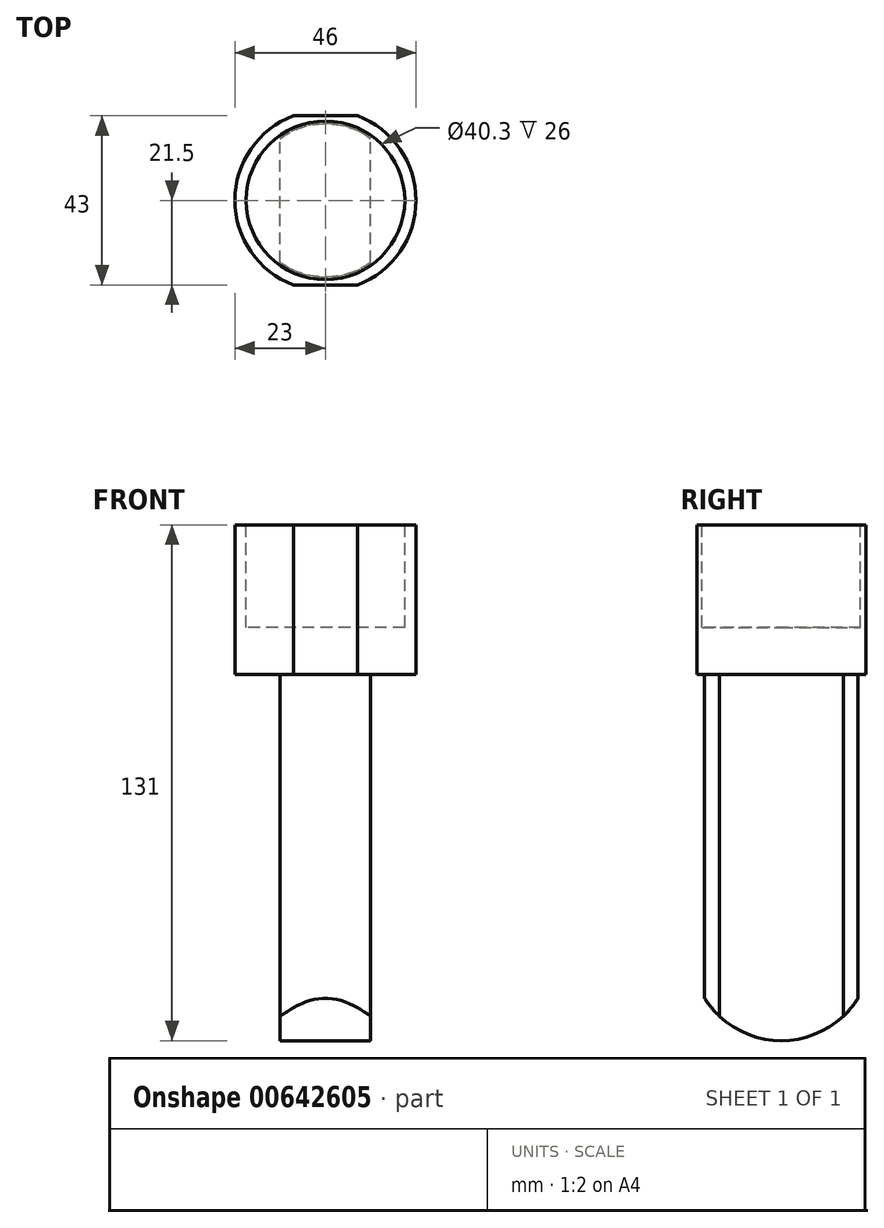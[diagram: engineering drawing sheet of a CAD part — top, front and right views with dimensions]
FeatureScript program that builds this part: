
annotation { "Feature Type Name" : "Feature", "Feature Type Description" : "" }
export const myFeature = defineFeature(function(context is Context, id is Id, definition is map)
    precondition{}
    {
        {
            var Q0;
            Q0=qCreatedBy(makeId("Top.planeOp"),FACE);
            var sketch = newSketch(context, id + "F0", { "sketchPlane" : qUnion([Q0])});
            skArc(sketch, "E0", {"start": v(-8.17, 21.5) * mm, "mid": v(-23, 0) * mm, "end": v(-8.17, -21.5) * mm});
            skLineSegment(sketch, "E1", {"start": v(-8.17, 21.5) * mm, "end": v(8.17, 21.5) * mm});
            skLineSegment(sketch, "E2.MirrorCS", {"start": v(-8.17, -21.5) * mm, "end": v(8.17, -21.5) * mm});
            skArc(sketch, "E3.trimOffspring", {"start": v(8.17, -21.5) * mm, "mid": v(23, 0) * mm, "end": v(8.17, 21.5) * mm});
            skSolve(sketch);
        }
        {
            var Q0;
            Q0 = qSketchRegion(id + "F0", true);
            extrude(context, id + "F1", {"entities" : qUnion([Q0]), "depth" : 38 * mm, "offsetDistance" : 25 * mm});
        }
        {
            var Q0;
            Q0=makeQuery(id+"F1.opExtrude","CAP_FACE",FACE,{"disambiguationData":[OSD([sQuery(id+"F0.wireOp",EDGE,"E0"),sQuery(id+"F0.wireOp",EDGE,"E1"),sQuery(id+"F0.wireOp",EDGE,"E2.MirrorCS"),sQuery(id+"F0.wireOp",EDGE,"E3.trimOffspring")])],"isStart":false});
            var sketch = newSketch(context, id + "F2", { "sketchPlane" : qUnion([Q0])});
            skCircle(sketch, "E4", {"center": v(0, 0) * mm, "radius": 20.15 * mm});
            skSolve(sketch);
        }
        {
            var Q0;
            Q0=makeQuery(id+"F2.imprint","IMPRINT",FACE,{"disambiguationData":[TD([[makeQuery(id+"F2.imprint","IMPRINT",EDGE,{"derivedFrom":sQuery(id+"F2.wireOp",EDGE,"E4")}),1.0]])]});
            extrude(context, id + "F3", {"entities" : qUnion([Q0]), "operationType" : NewBodyOperationType.REMOVE, "oppositeDirection" : true, "depth" : 26 * mm, "offsetDistance" : 25 * mm});
        }
        {
            var Q0;
            Q0=makeQuery(id+"F1.opExtrude","CAP_FACE",FACE,{"disambiguationData":[OSD([sQuery(id+"F0.wireOp",EDGE,"E0"),sQuery(id+"F0.wireOp",EDGE,"E1"),sQuery(id+"F0.wireOp",EDGE,"E2.MirrorCS"),sQuery(id+"F0.wireOp",EDGE,"E3.trimOffspring")])],"isStart":true});
            var sketch = newSketch(context, id + "F4", { "sketchPlane" : qUnion([Q0])});
            skArc(sketch, "E5", {"start": v(11.5, 15.75) * mm, "mid": v(0, 19.5) * mm, "end": v(-11.5, 15.75) * mm});
            skLineSegment(sketch, "E6", {"start": v(-11.5, 15.75) * mm, "end": v(-11.5, -15.75) * mm});
            skLineSegment(sketch, "E7.MirrorCS", {"start": v(11.5, 15.75) * mm, "end": v(11.5, -15.75) * mm});
            skArc(sketch, "E8.trimOffspring", {"start": v(-11.5, -15.75) * mm, "mid": v(0, -19.5) * mm, "end": v(11.5, -15.75) * mm});
            skSolve(sketch);
        }
        {
            var Q0;
            Q0=makeQuery(id+"F4.imprint","IMPRINT",FACE,{"disambiguationData":[TD([[makeQuery(id+"F4.imprint","IMPRINT",EDGE,{"derivedFrom":sQuery(id+"F4.wireOp",EDGE,"E5")}),1.0]])]});
            extrude(context, id + "F5", {"entities" : qUnion([Q0]), "operationType" : NewBodyOperationType.ADD, "depth" : 93 * mm, "offsetDistance" : 25 * mm});
        }
        {
            var Q0;
            Q0=makeQuery(id+"F5.opExtrude","SWEPT_FACE",FACE,{"disambiguationData":[OSD([sQuery(id+"F4.wireOp",EDGE,"E7.MirrorCS")])]});
            var sketch = newSketch(context, id + "F6", { "sketchPlane" : qUnion([Q0])});
            skArc(sketch, "E9", {"start": v(-22.95, -68.43) * mm, "mid": v(-5.38, -92.36) * mm, "end": v(21.15, -79.04) * mm});
            skLineSegment(sketch, "E10", {"start": v(-22.95, -68.43) * mm, "end": v(-27.64, -129.07) * mm});
            skLineSegment(sketch, "E11", {"start": v(-27.64, -129.07) * mm, "end": v(47.57, -125.6) * mm});
            skLineSegment(sketch, "E12", {"start": v(47.57, -125.6) * mm, "end": v(21.15, -79.04) * mm});
            skSolve(sketch);
        }
        {
            var Q0;
            {var subQ0=sQuery(id+"F6.wireOp",EDGE,"E9");var subQ1=sQuery(id+"F4.wireOp",EDGE,"E7.MirrorCS");var subQ4=makeQuery(id+"F5.opExtrude","CAP_EDGE",EDGE,{"disambiguationData":[OSD([subQ1])],"isStart":false});var subQ5=makeQuery(id+"F6.imprint","INTERSECT",VERTEX,{"derivedFrom":[subQ4,subQ0]});Q0=makeQuery(id+"F6.imprint","IMPRINT",FACE,{"disambiguationData":[TD([[makeQuery(id+"F6.imprint","IMPRINT",EDGE,{"disambiguationData":[TD([[subQ5,1.0]])],"derivedFrom":subQ0}),-1.0]])]});}
            var Q1;
            {var subQ0=sQuery(id+"F6.wireOp",EDGE,"E9");var subQ1=sQuery(id+"F4.wireOp",EDGE,"E7.MirrorCS");var subQ4=makeQuery(id+"F5.opExtrude","CAP_EDGE",EDGE,{"disambiguationData":[OSD([subQ1])],"isStart":false});var subQ5=makeQuery(id+"F6.imprint","INTERSECT",VERTEX,{"derivedFrom":[subQ4,subQ0]});Q1=makeQuery(id+"F6.imprint","IMPRINT",FACE,{"disambiguationData":[TD([[makeQuery(id+"F6.imprint","IMPRINT",EDGE,{"disambiguationData":[TD([[subQ5,-1.0]])],"derivedFrom":subQ0}),-1.0]])]});}
            var Q2;
            {var subQ0=sQuery(id+"F6.wireOp",EDGE,"E10");Q2=makeQuery(id+"F6.imprint","IMPRINT",FACE,{"disambiguationData":[TD([[makeQuery(id+"F6.imprint","IMPRINT",EDGE,{"derivedFrom":subQ0}),1.0]])]});}
            extrude(context, id + "F7", {"entities" : qUnion([Q0, Q1, Q2]), "operationType" : NewBodyOperationType.REMOVE, "endBound" : BoundingType.THROUGH_ALL, "oppositeDirection" : true, "depth" : 25 * mm, "offsetDistance" : 25 * mm});
        }
    });
